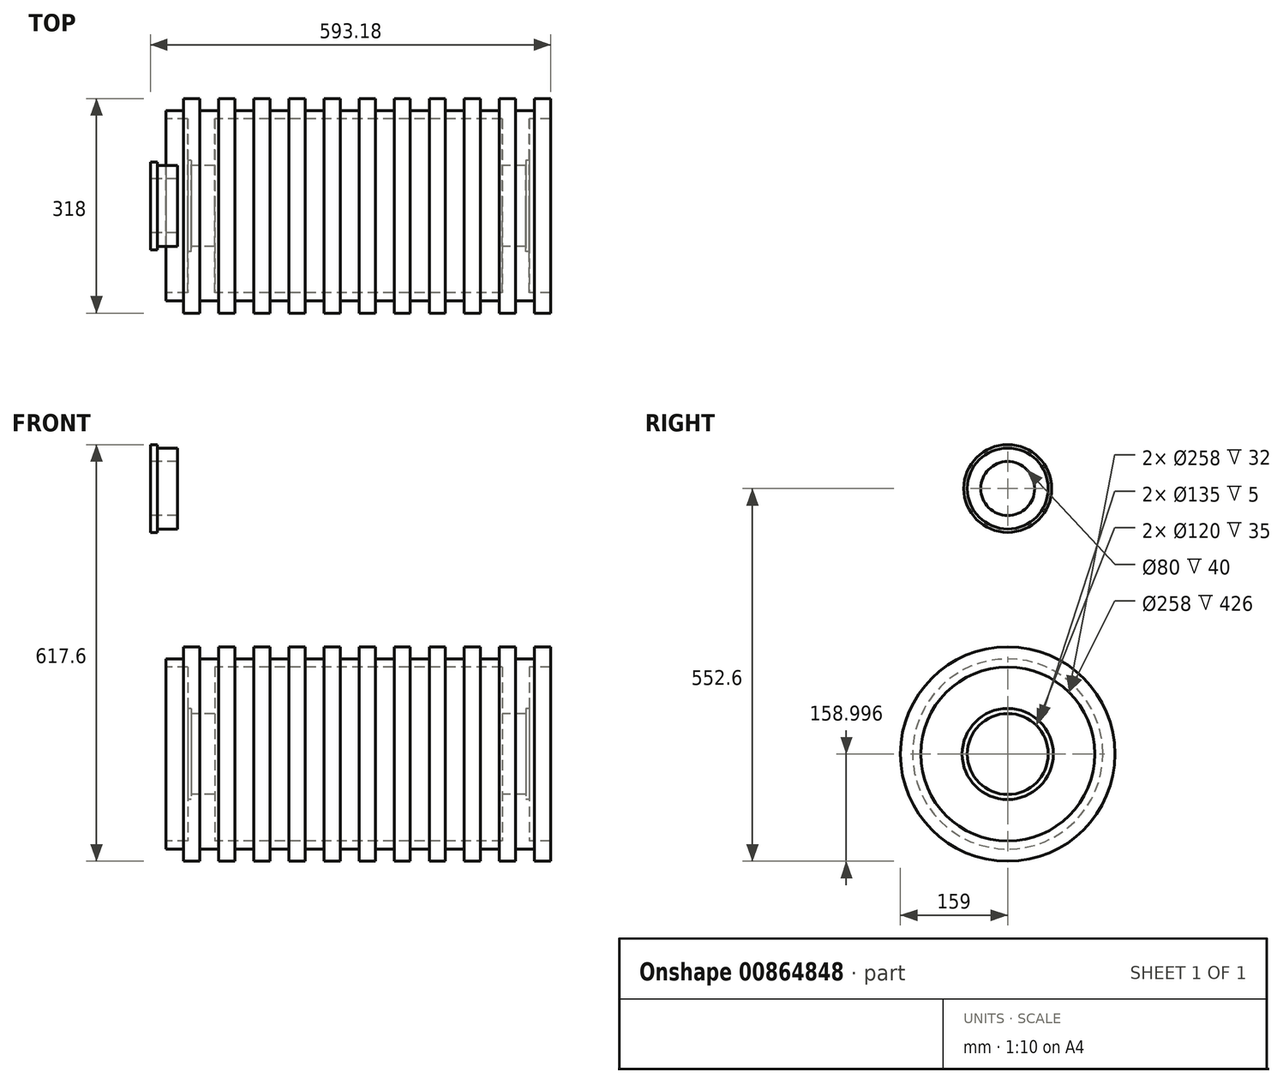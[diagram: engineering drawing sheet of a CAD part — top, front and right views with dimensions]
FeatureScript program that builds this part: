
annotation { "Feature Type Name" : "Feature", "Feature Type Description" : "" }
export const myFeature = defineFeature(function(context is Context, id is Id, definition is map)
    precondition{}
    {
        {
            var Q0;
            Q0=qCreatedBy(makeId("Front.planeOp"),FACE);
            var sketch = newSketch(context, id + "F0", { "sketchPlane" : qUnion([Q0])});
            skLineSegment(sketch, "E0", {"start": v(23.18, -264.6) * mm, "end": v(55.18, -264.6) * mm});
            skLineSegment(sketch, "E1.0", {"start": v(23.18, -252.6) * mm, "end": v(49.18, -252.6) * mm});
            skLineSegment(sketch, "E2.0", {"start": v(49.18, -234.6) * mm, "end": v(73.18, -234.6) * mm});
            skLineSegment(sketch, "E3", {"start": v(23.18, -252.6) * mm, "end": v(23.18, -264.6) * mm});
            skLineSegment(sketch, "E4.0", {"start": v(49.18, -234.6) * mm, "end": v(49.18, -252.6) * mm});
            skLineSegment(sketch, "E5.0", {"start": v(73.18, -234.6) * mm, "end": v(73.18, -252.6) * mm});
            skLineSegment(sketch, "E6.0", {"start": v(101.18, -234.6) * mm, "end": v(101.18, -252.6) * mm});
            skLineSegment(sketch, "E7.0", {"start": v(125.18, -234.6) * mm, "end": v(125.18, -252.6) * mm});
            skLineSegment(sketch, "E8.trimOffspring", {"start": v(101.18, -234.6) * mm, "end": v(125.18, -234.6) * mm});
            skLineSegment(sketch, "E9.0", {"start": v(153.18, -234.6) * mm, "end": v(153.18, -252.6) * mm});
            skLineSegment(sketch, "E10.0", {"start": v(177.18, -234.6) * mm, "end": v(177.18, -252.6) * mm});
            skLineSegment(sketch, "E11.0", {"start": v(205.18, -234.6) * mm, "end": v(205.18, -252.6) * mm});
            skLineSegment(sketch, "E12.0", {"start": v(229.18, -234.6) * mm, "end": v(229.18, -252.6) * mm});
            skLineSegment(sketch, "E13.trimOffspring", {"start": v(153.18, -234.6) * mm, "end": v(177.18, -234.6) * mm});
            skLineSegment(sketch, "E14.trimOffspring", {"start": v(205.18, -234.6) * mm, "end": v(229.18, -234.6) * mm});
            skLineSegment(sketch, "E15.0", {"start": v(257.18, -234.6) * mm, "end": v(257.18, -252.6) * mm});
            skLineSegment(sketch, "E16.0", {"start": v(281.18, -234.6) * mm, "end": v(281.18, -252.6) * mm});
            skLineSegment(sketch, "E17.0", {"start": v(309.18, -234.6) * mm, "end": v(309.18, -252.6) * mm});
            skLineSegment(sketch, "E18.0", {"start": v(333.18, -234.6) * mm, "end": v(333.18, -252.6) * mm});
            skLineSegment(sketch, "E19.0", {"start": v(361.18, -234.6) * mm, "end": v(361.18, -252.6) * mm});
            skLineSegment(sketch, "E20.0", {"start": v(385.18, -234.6) * mm, "end": v(385.18, -252.6) * mm});
            skLineSegment(sketch, "E21.0", {"start": v(413.18, -234.6) * mm, "end": v(413.18, -252.6) * mm});
            skLineSegment(sketch, "E22.0", {"start": v(437.18, -234.6) * mm, "end": v(437.18, -252.6) * mm});
            skLineSegment(sketch, "E23.0", {"start": v(465.18, -234.6) * mm, "end": v(465.18, -252.6) * mm});
            skLineSegment(sketch, "E24.0", {"start": v(489.18, -234.6) * mm, "end": v(489.18, -252.6) * mm});
            skLineSegment(sketch, "E25.0", {"start": v(517.18, -234.6) * mm, "end": v(517.18, -252.6) * mm});
            skLineSegment(sketch, "E26.0", {"start": v(541.18, -234.6) * mm, "end": v(541.18, -252.6) * mm});
            skLineSegment(sketch, "E27.0", {"start": v(569.18, -234.6) * mm, "end": v(569.18, -252.6) * mm});
            skLineSegment(sketch, "E28.0", {"start": v(593.18, -234.6) * mm, "end": v(593.18, -252.6) * mm});
            skLineSegment(sketch, "E29.trimOffspring", {"start": v(569.18, -234.6) * mm, "end": v(593.18, -234.6) * mm});
            skLineSegment(sketch, "E30.trimOffspring", {"start": v(517.18, -234.6) * mm, "end": v(541.18, -234.6) * mm});
            skLineSegment(sketch, "E31.trimOffspring", {"start": v(465.18, -234.6) * mm, "end": v(489.18, -234.6) * mm});
            skLineSegment(sketch, "E32.trimOffspring", {"start": v(413.18, -234.6) * mm, "end": v(437.18, -234.6) * mm});
            skLineSegment(sketch, "E33.trimOffspring", {"start": v(361.18, -234.6) * mm, "end": v(385.18, -234.6) * mm});
            skLineSegment(sketch, "E34.trimOffspring", {"start": v(309.18, -234.6) * mm, "end": v(333.18, -234.6) * mm});
            skLineSegment(sketch, "E35.trimOffspring", {"start": v(257.18, -234.6) * mm, "end": v(281.18, -234.6) * mm});
            skLineSegment(sketch, "E36", {"start": v(593.18, -252.6) * mm, "end": v(593.18, -264.6) * mm});
            skLineSegment(sketch, "E37.0", {"start": v(23.18, -393.6) * mm, "end": v(593.18, -393.6) * mm});
            skLineSegment(sketch, "E38.0", {"start": v(55.18, -264.6) * mm, "end": v(55.18, -326.1) * mm});
            skLineSegment(sketch, "E39.0", {"start": v(561.18, -264.6) * mm, "end": v(561.18, -326.1) * mm});
            skLineSegment(sketch, "E40.trimOffspring", {"start": v(561.18, -264.6) * mm, "end": v(593.18, -264.6) * mm});
            skLineSegment(sketch, "E41.0", {"start": v(60.18, -333.6) * mm, "end": v(95.18, -333.6) * mm});
            skLineSegment(sketch, "E42.0", {"start": v(55.18, -326.1) * mm, "end": v(60.18, -326.1) * mm});
            skLineSegment(sketch, "E43.0", {"start": v(60.18, -326.1) * mm, "end": v(60.18, -333.6) * mm});
            skLineSegment(sketch, "E44.0", {"start": v(556.18, -326.1) * mm, "end": v(556.18, -333.6) * mm});
            skLineSegment(sketch, "E45.0", {"start": v(95.18, -264.6) * mm, "end": v(95.18, -333.6) * mm});
            skLineSegment(sketch, "E46.0", {"start": v(521.18, -264.6) * mm, "end": v(521.18, -333.6) * mm});
            skLineSegment(sketch, "E47.trimOffspring", {"start": v(556.18, -326.1) * mm, "end": v(561.18, -326.1) * mm});
            skLineSegment(sketch, "E48.trimOffspring", {"start": v(521.18, -333.6) * mm, "end": v(556.18, -333.6) * mm});
            skLineSegment(sketch, "E49", {"start": v(95.18, -264.6) * mm, "end": v(521.18, -264.6) * mm});
            skLineSegment(sketch, "E50.trimOffspring", {"start": v(73.18, -252.6) * mm, "end": v(101.18, -252.6) * mm});
            skLineSegment(sketch, "E51.trimOffspring", {"start": v(125.18, -252.6) * mm, "end": v(153.18, -252.6) * mm});
            skLineSegment(sketch, "E52.trimOffspring", {"start": v(177.18, -252.6) * mm, "end": v(205.18, -252.6) * mm});
            skLineSegment(sketch, "E53.trimOffspring", {"start": v(229.18, -252.6) * mm, "end": v(257.18, -252.6) * mm});
            skLineSegment(sketch, "E54.trimOffspring", {"start": v(281.18, -252.6) * mm, "end": v(309.18, -252.6) * mm});
            skLineSegment(sketch, "E55.trimOffspring", {"start": v(333.18, -252.6) * mm, "end": v(361.18, -252.6) * mm});
            skLineSegment(sketch, "E56.trimOffspring", {"start": v(385.18, -252.6) * mm, "end": v(413.18, -252.6) * mm});
            skLineSegment(sketch, "E57.trimOffspring", {"start": v(437.18, -252.6) * mm, "end": v(465.18, -252.6) * mm});
            skLineSegment(sketch, "E58.trimOffspring", {"start": v(489.18, -252.6) * mm, "end": v(517.18, -252.6) * mm});
            skLineSegment(sketch, "E59.trimOffspring", {"start": v(541.18, -252.6) * mm, "end": v(569.18, -252.6) * mm});
            skSolve(sketch);
        }
        {
            var Q0;
            Q0=makeQuery(id+"F0.imprint","IMPRINT",FACE,{"disambiguationData":[TD([[makeQuery(id+"F0.imprint","IMPRINT",EDGE,{"derivedFrom":sQuery(id+"F0.wireOp",EDGE,"E0")}),1.0]])]});
            var Q1;
            Q1=sQuery(id+"F0.wireOp",EDGE,"E37.0");
            revolve(context, id + "F1", {"surfaceOperationType" : NewSurfaceOperationType.NEW, "entities" : qUnion([Q0]), "axis" : qUnion([Q1]), "revolveType" : RevolveType.FULL});
        }
        {
            var Q0;
            Q0=qCreatedBy(makeId("Front.planeOp"),FACE);
            var sketch = newSketch(context, id + "F2", { "sketchPlane" : qUnion([Q0])});
            skLineSegment(sketch, "E60", {"start": v(0, 0) * mm, "end": v(648.86, 0) * mm});
            skLineSegment(sketch, "E61.0", {"start": v(0, 60) * mm, "end": v(40, 60) * mm});
            skLineSegment(sketch, "E62.0", {"start": v(0, 65) * mm, "end": v(10, 65) * mm});
            skLineSegment(sketch, "E63", {"start": v(0, 40) * mm, "end": v(0, 65) * mm});
            skLineSegment(sketch, "E64.0", {"start": v(0, 40) * mm, "end": v(40, 40) * mm});
            skLineSegment(sketch, "E65.0", {"start": v(10, 40) * mm, "end": v(10, 65) * mm});
            skLineSegment(sketch, "E66.0", {"start": v(40, 40) * mm, "end": v(40, 60) * mm});
            skLineSegment(sketch, "E67.0", {"start": v(0, 55) * mm, "end": v(40, 55) * mm});
            skLineSegment(sketch, "E68.0", {"start": v(0, 45) * mm, "end": v(40, 45) * mm});
            skSolve(sketch);
        }
        {
            var Q0;
            {var subQ5=sQuery(id+"F2.wireOp",EDGE,"E62.0");Q0=makeQuery(id+"F2.imprint","IMPRINT",FACE,{"disambiguationData":[TD([[makeQuery(id+"F2.imprint","IMPRINT",EDGE,{"derivedFrom":subQ5}),-1.0]])]});}
            var Q1;
            {var subQ0=sQuery(id+"F2.wireOp",EDGE,"E63");var subQ1=sQuery(id+"F2.wireOp",EDGE,"E61.0");var subQ2=makeQuery(id+"F2.imprint","INTERSECT",VERTEX,{"derivedFrom":[subQ1,subQ0]});Q1=makeQuery(id+"F2.imprint","IMPRINT",FACE,{"disambiguationData":[TD([[makeQuery(id+"F2.imprint","IMPRINT",EDGE,{"disambiguationData":[TD([[subQ2,-1.0]])],"derivedFrom":subQ1}),-1.0]])]});}
            var Q2;
            {var subQ0=sQuery(id+"F2.wireOp",EDGE,"E66.0");var subQ1=sQuery(id+"F2.wireOp",EDGE,"E61.0");var subQ2=makeQuery(id+"F2.imprint","INTERSECT",VERTEX,{"derivedFrom":[subQ1,subQ0]});Q2=makeQuery(id+"F2.imprint","IMPRINT",FACE,{"disambiguationData":[TD([[makeQuery(id+"F2.imprint","IMPRINT",EDGE,{"disambiguationData":[TD([[subQ2,1.0]])],"derivedFrom":subQ1}),-1.0]])]});}
            var Q3;
            {var subQ0=sQuery(id+"F2.wireOp",EDGE,"E68.0");var subQ1=sQuery(id+"F2.wireOp",EDGE,"E65.0");var subQ2=makeQuery(id+"F2.imprint","INTERSECT",VERTEX,{"derivedFrom":[subQ1,subQ0]});Q3=makeQuery(id+"F2.imprint","IMPRINT",FACE,{"disambiguationData":[TD([[makeQuery(id+"F2.imprint","IMPRINT",EDGE,{"disambiguationData":[TD([[subQ2,-1.0]])],"derivedFrom":subQ1}),-1.0]])]});}
            var Q4;
            {var subQ0=sQuery(id+"F2.wireOp",EDGE,"E67.0");var subQ1=sQuery(id+"F2.wireOp",EDGE,"E63");var subQ2=makeQuery(id+"F2.imprint","INTERSECT",VERTEX,{"derivedFrom":[subQ1,subQ0]});Q4=makeQuery(id+"F2.imprint","IMPRINT",FACE,{"disambiguationData":[TD([[makeQuery(id+"F2.imprint","IMPRINT",EDGE,{"disambiguationData":[TD([[subQ2,1.0]])],"derivedFrom":subQ1}),-1.0]])]});}
            var Q5;
            {var subQ0=sQuery(id+"F2.wireOp",EDGE,"E64.0");var subQ1=sQuery(id+"F2.wireOp",EDGE,"E63");var subQ2=makeQuery(id+"F2.imprint","INTERSECT",VERTEX,{"derivedFrom":[subQ1,subQ0]});Q5=makeQuery(id+"F2.imprint","IMPRINT",FACE,{"disambiguationData":[TD([[makeQuery(id+"F2.imprint","IMPRINT",EDGE,{"disambiguationData":[TD([[subQ2,-1.0]])],"derivedFrom":subQ1}),-1.0]])]});}
            var Q6;
            {var subQ0=sQuery(id+"F2.wireOp",EDGE,"E66.0");var subQ1=sQuery(id+"F2.wireOp",EDGE,"E64.0");var subQ2=makeQuery(id+"F2.imprint","INTERSECT",VERTEX,{"derivedFrom":[subQ1,subQ0]});Q6=makeQuery(id+"F2.imprint","IMPRINT",FACE,{"disambiguationData":[TD([[makeQuery(id+"F2.imprint","IMPRINT",EDGE,{"disambiguationData":[TD([[subQ2,1.0]])],"derivedFrom":subQ1}),1.0]])]});}
            var Q7;
            Q7=sQuery(id+"F2.wireOp",EDGE,"E60");
            revolve(context, id + "F3", {"surfaceOperationType" : NewSurfaceOperationType.NEW, "entities" : qUnion([Q0, Q1, Q2, Q3, Q4, Q5, Q6]), "axis" : qUnion([Q7]), "revolveType" : RevolveType.FULL});
        }
    });
